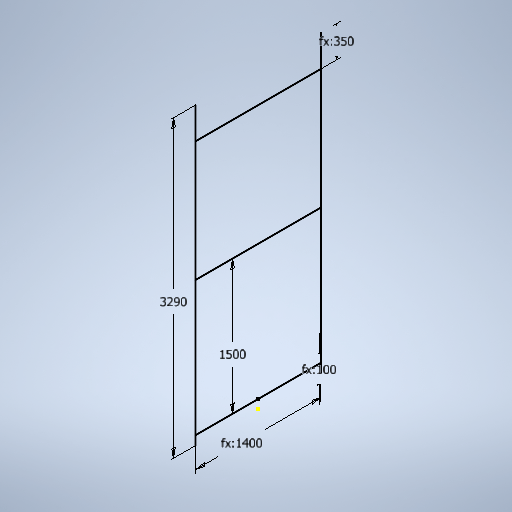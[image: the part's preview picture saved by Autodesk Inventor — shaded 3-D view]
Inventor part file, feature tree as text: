
AUTODESK INVENTOR PART (.ipt)
format: ipt  version: 2025 (Build 290162010, 162A)  size: 264,192 bytes
history: native  units: mm
features: sketch x1
ambient origin geometry x8: Origin, YZ Plane, XZ Plane, XY Plane, X Axis, Y Axis, Z Axis, Center Point
feature tree (1):
  sketch  "Sketch2"  dims[d4=3290.0mm d5=1400.0mm d6=350.0mm d7=100.0mm d8=1500.0mm]
